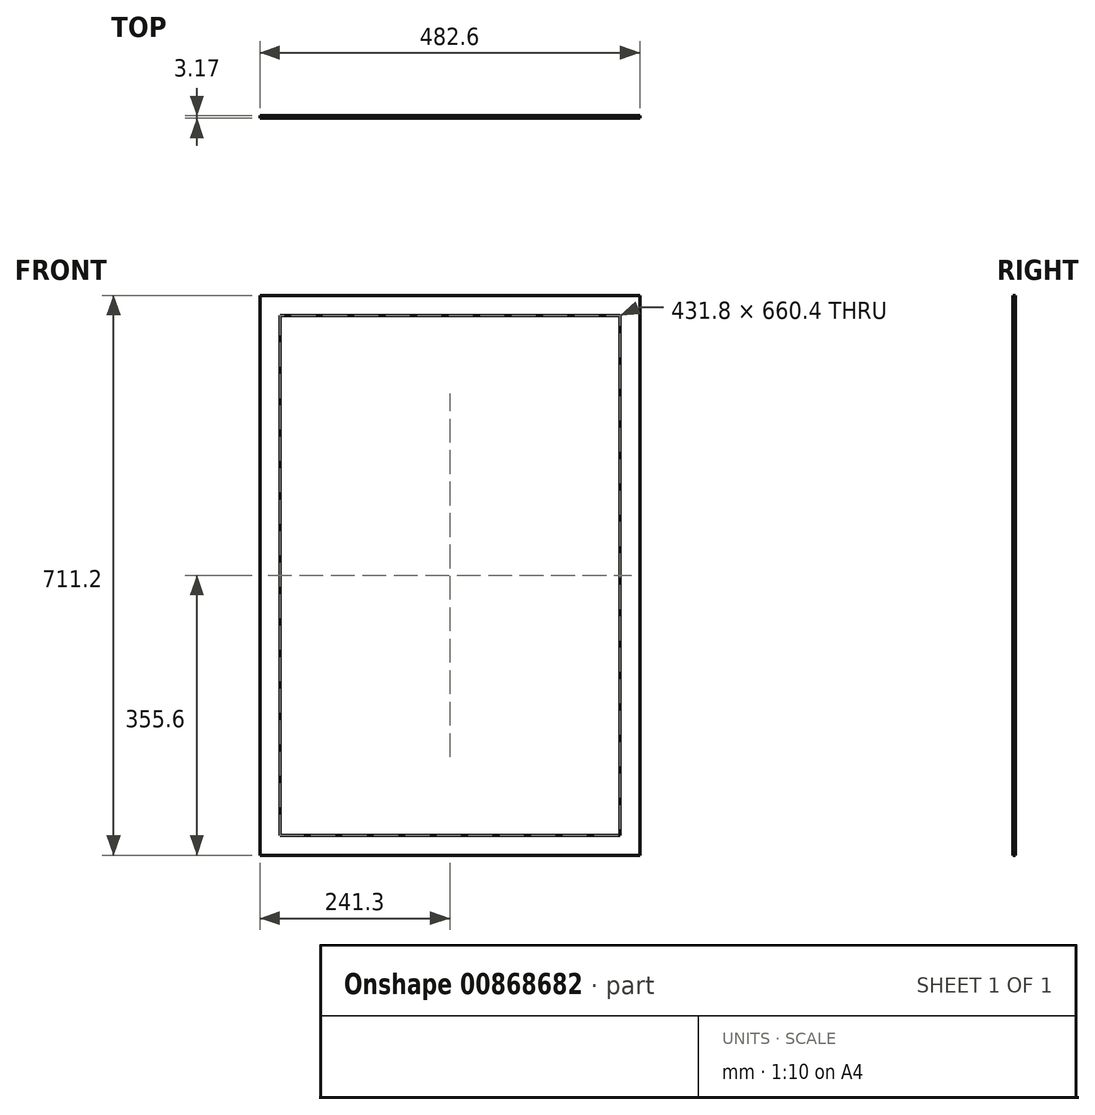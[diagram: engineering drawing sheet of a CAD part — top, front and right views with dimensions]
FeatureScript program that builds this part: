
annotation { "Feature Type Name" : "Feature", "Feature Type Description" : "" }
export const myFeature = defineFeature(function(context is Context, id is Id, definition is map)
    precondition{}
    {
        {
            var Q0;
            Q0=qCreatedBy(makeId("Front.planeOp"),FACE);
            var sketch = newSketch(context, id + "F0", { "sketchPlane" : qUnion([Q0])});
            skLineSegment(sketch, "E0.bottom", {"start": v(-241.3, 342.9) * mm, "end": v(-215.9, 342.9) * mm});
            skLineSegment(sketch, "E0.top", {"start": v(-241.3, -342.9) * mm, "end": v(-215.9, -342.9) * mm});
            skLineSegment(sketch, "E0.left", {"start": v(-241.3, 342.9) * mm, "end": v(-241.3, -342.9) * mm});
            skLineSegment(sketch, "E0.right", {"start": v(-215.9, 342.9) * mm, "end": v(-215.9, -342.9) * mm});
            skPoint(sketch, "E0.middle", {"position": v(-228.6, 0) * mm});
            skLineSegment(sketch, "E1", {"start": v(-215.9, -342.9) * mm, "end": v(0, -342.9) * mm});
            skPoint(sketch, "E2.MirrorP", {"position": v(228.6, 0) * mm});
            skLineSegment(sketch, "E3.MirrorCS", {"start": v(215.9, 342.9) * mm, "end": v(215.9, -342.9) * mm});
            skLineSegment(sketch, "E4.MirrorCS", {"start": v(241.3, 342.9) * mm, "end": v(241.3, -342.9) * mm});
            skLineSegment(sketch, "E5.MirrorCS", {"start": v(215.9, -342.9) * mm, "end": v(0, -342.9) * mm});
            skLineSegment(sketch, "E6.MirrorCS", {"start": v(241.3, 342.9) * mm, "end": v(215.9, 342.9) * mm});
            skLineSegment(sketch, "E7.MirrorCS", {"start": v(241.3, -342.9) * mm, "end": v(215.9, -342.9) * mm});
            skLineSegment(sketch, "E8", {"start": v(-215.9, -317.5) * mm, "end": v(215.9, -317.5) * mm});
            skLineSegment(sketch, "E9.bottom", {"start": v(-241.3, 342.9) * mm, "end": v(241.3, 342.9) * mm});
            skLineSegment(sketch, "E9.top", {"start": v(-241.3, 368.3) * mm, "end": v(241.3, 368.3) * mm});
            skLineSegment(sketch, "E9.left", {"start": v(-241.3, 342.9) * mm, "end": v(-241.3, 368.3) * mm});
            skLineSegment(sketch, "E9.right", {"start": v(241.3, 342.9) * mm, "end": v(241.3, 368.3) * mm});
            skSolve(sketch);
        }
        {
            var Q0;
            Q0 = qSketchRegion(id + "F0", true);
            extrude(context, id + "F1", {"entities" : qUnion([Q0]), "depth" : 3.17 * mm, "offsetDistance" : 25.4 * mm});
        }
    });
